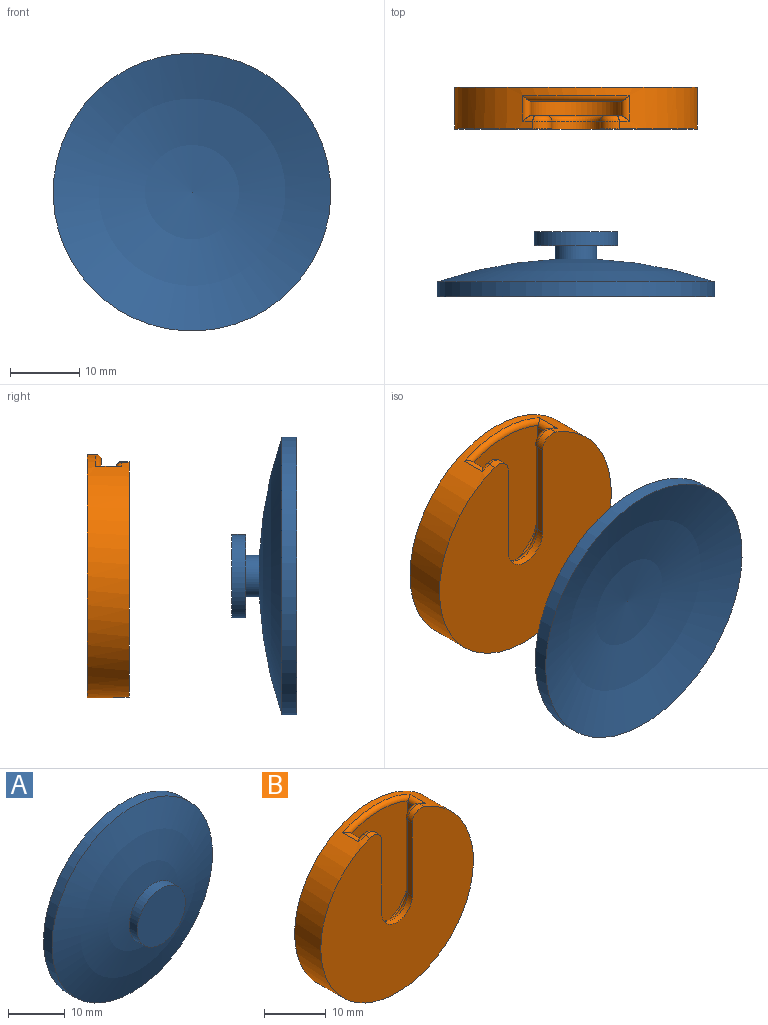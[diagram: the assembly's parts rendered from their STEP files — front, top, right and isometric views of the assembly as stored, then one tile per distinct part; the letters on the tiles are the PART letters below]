
ASSEMBLY  parts=2 mates=1
PART A: 7 faces, bbox 40x9.4x40 mm
  f0: cylinder r=6mm len=12mm, axis (0,-1,0), area 75.4mm2, adj f1,f6
  f1: plane 12x12mm, normal (0,-1,0), area 113.1mm2, adj f0
  f2: sphere r=60mm, area 1293.6mm2, adj f3
  f3: cylinder r=20mm len=40mm, axis (0,-1,0), area 266mm2, adj f2,f4
  f4: sphere r=62mm, area 1262.9mm2, adj f3,f5
  f5: cylinder r=3mm len=6mm, axis (0,-1,0), area 37.7mm2, adj f4,f6
  f6: plane 12x12mm, normal (0,1,0), area 84.8mm2, adj f0,f5
PART B: 23 faces, bbox 35x6x36.4 mm
  f0: cylinder r=17.5mm len=35mm, axis (0,1,0), area 587.2mm2, adj f1,f3,f11,f12,f14,f16,f18,f20
  f1: plane 35x33.99mm, normal (0,-1,0), area 817.8mm2, adj f0,f8,f9,f10,f11,f12
  f2: plane 22.19x13.14mm, normal (0,1,0), area 105.5mm2, adj f4,f5,f7,f13,f14,f15,f16,f17
  f3: plane 35x35mm, normal (0,1,0), area 962.1mm2, adj f0
  f4: plane 15.02x2.1mm, normal (1,0,0), area 31.5mm2, adj f2,f6,f7,f16
  f5: plane 15.02x2.1mm, normal (-1,0,0), area 31.5mm2, adj f2,f6,f7,f20
  f6: plane 23.2x13.14mm, normal (0,-1,0), area 277.9mm2, adj f4,f5,f7,f16,f18,f20
  f7: cylinder r=6.5mm len=13mm, axis (0,1,0), area 42.9mm2, adj f2,f4,f5,f6
  f8: cylinder r=3.5mm len=7mm, axis (0,-1,0), area 12.1mm2, adj f1,f9,f10,f17
  f9: plane 14.49x1.1mm, normal (-1,0,0), area 15.9mm2, adj f1,f8,f11,f19
  f10: plane 14.49x1.1mm, normal (1,0,0), area 15.9mm2, adj f1,f8,f12,f15
  f11: cylinder r=2mm len=2.71mm, axis (0,1,0), area 4.3mm2, adj f0,f1,f9,f21
  f12: cylinder r=2mm len=2.71mm, axis (0,1,0), area 4.3mm2, adj f0,f1,f10,f13
  f13: torus R=1.2mm, axis (0,-1,0), area 4.2mm2, adj f2,f12,f14,f15
  f14: torus R=16.7mm, axis (0,-1,0), area 1.3mm2, adj f0,f2,f13,f16
  f15: cylinder r=0.8mm len=14.49mm, axis (0,0,-1), area 18.2mm2, adj f2,f10,f13,f17
  f16: cylinder r=0.8mm len=3.7mm, axis (0,1,0), area 4.1mm2, adj f0,f2,f4,f6,f14,f18
  f17: torus R=4.3mm, axis (0,-1,0), area 15mm2, adj f2,f8,f15,f19
  f18: torus R=16.7mm, axis (0,-1,0), area 18.3mm2, adj f0,f6,f16,f20
  f19: cylinder r=0.8mm len=14.49mm, axis (0,0,1), area 18.2mm2, adj f2,f9,f17,f21
  f20: cylinder r=0.8mm len=3.7mm, axis (0,1,0), area 4.1mm2, adj f0,f2,f5,f6,f18,f22
  f21: torus R=1.2mm, axis (0,-1,0), area 4.2mm2, adj f2,f11,f19,f22
  f22: torus R=16.7mm, axis (0,-1,0), area 1.3mm2, adj f0,f2,f20,f21
PLACE A rot(axis=(1,0,0),180deg) t=(0,-9,0)mm
PLACE B at identity
MATE parallel A.f0 <-> B.f7  axis (0,1,0) through (0,-20.77,0)mm
